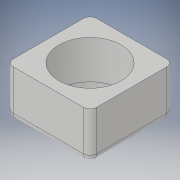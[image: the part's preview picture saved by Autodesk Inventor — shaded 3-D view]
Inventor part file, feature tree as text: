
AUTODESK INVENTOR PART (.ipt)
format: ipt  version: 2019 (Build 230136000, 136)  size: 136,704 bytes
history: native  units: in
note: dims shown in document units (in); Inventor stores cm internally (conversion verified against a paired STEP export)
features: fillet x2, sketch x2, extrude x1, plane x1, revolve x1
ambient origin geometry x8: Origin, YZ Plane, XZ Plane, XY Plane, X Axis, Y Axis, Z Axis, Center Point
bodies: Solid1 (feature_tree)
feature tree (7):
  extrude  "Extrusion1"  Depth=0.765in
  plane  "Work Plane2"
  revolve  "Revolution1"  [1 undecoded]
  fillet  "Fillet1"  [1 undecoded]
  fillet  "Fillet2"  Radius=0.0625in
  sketch  "Sketch1"  dims[d0=0.765in d1=0.765in]
  sketch  "Sketch2"  dims[d2=0.43in d3=0.0in d4=0.57in d5=90.0deg d6=0.0625in d7=0.0625in]
note: 2 required parameter values undecoded (feature->parameter linkage not recoverable at this tier; creation-order binding heuristic only, values carry confidence <= 0.55)